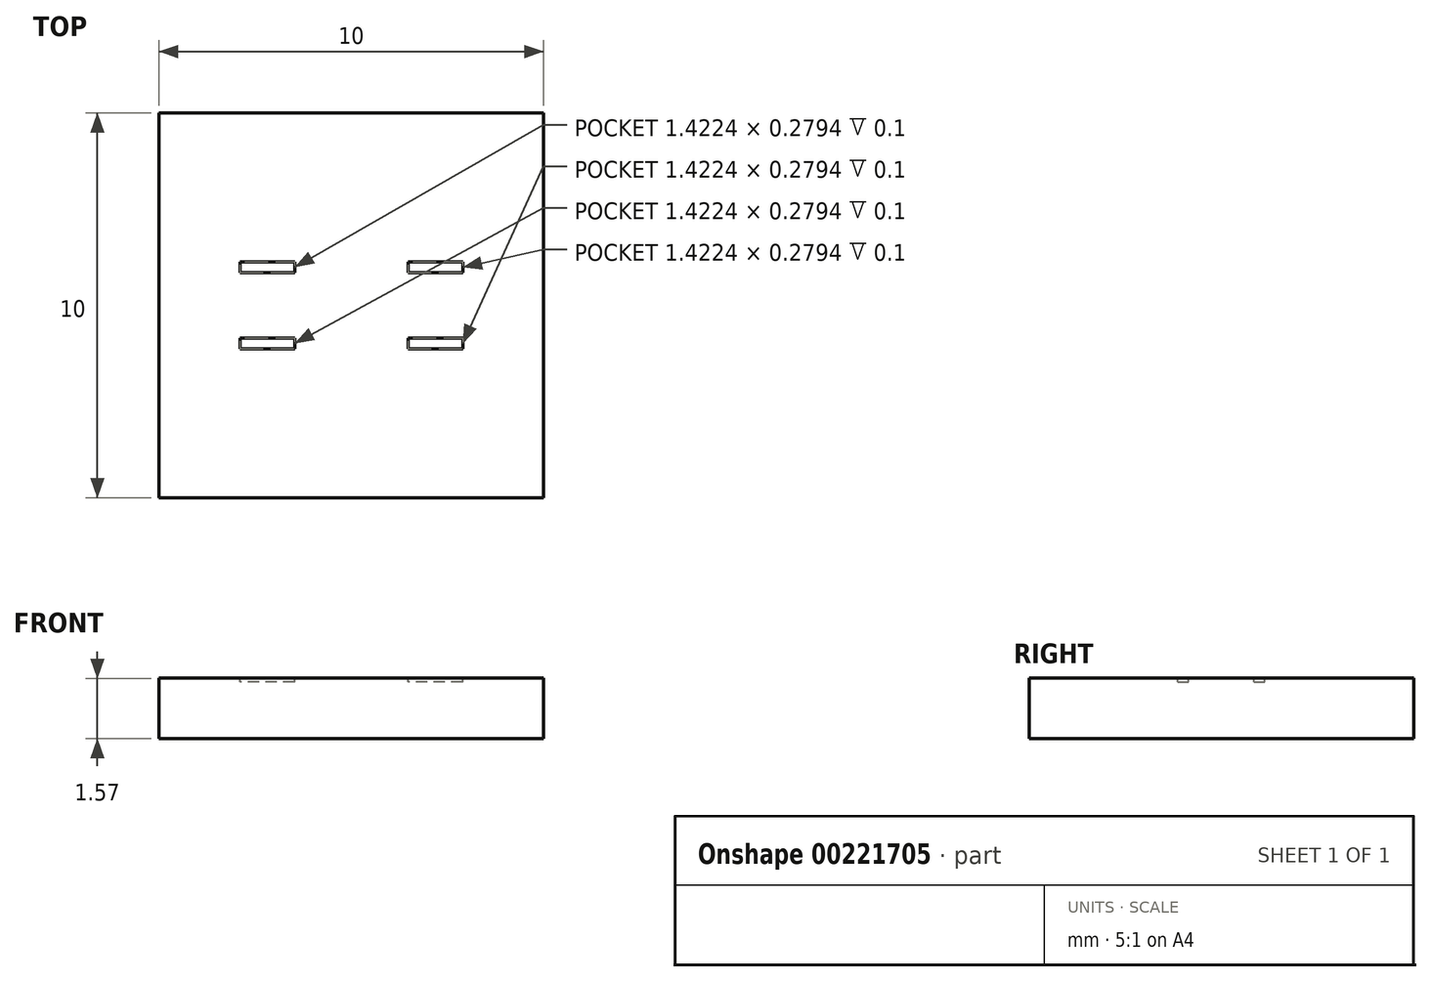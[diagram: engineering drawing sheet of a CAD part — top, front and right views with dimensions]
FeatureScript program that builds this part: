
annotation { "Feature Type Name" : "Feature", "Feature Type Description" : "" }
export const myFeature = defineFeature(function(context is Context, id is Id, definition is map)
    precondition{}
    {
        {
            var Q0;
            Q0=qCreatedBy(makeId("Top.planeOp"),FACE);
            var sketch = newSketch(context, id + "F0", { "sketchPlane" : qUnion([Q0])});
            skLineSegment(sketch, "E0.bottom", {"start": v(5, 5) * mm, "end": v(-5, 5) * mm});
            skLineSegment(sketch, "E0.top", {"start": v(5, -5) * mm, "end": v(-5, -5) * mm});
            skLineSegment(sketch, "E0.left", {"start": v(5, 5) * mm, "end": v(5, -5) * mm});
            skLineSegment(sketch, "E0.right", {"start": v(-5, 5) * mm, "end": v(-5, -5) * mm});
            skPoint(sketch, "E0.middle", {"position": v(0, 0) * mm});
            skSolve(sketch);
        }
        {
            var Q0;
            Q0 = qSketchRegion(id + "F0", true);
            extrude(context, id + "F1", {"entities" : qUnion([Q0]), "depth" : 1.57 * mm});
        }
        {
            var Q0;
            Q0=makeQuery(id+"F1.opExtrude","CAP_FACE",FACE,{"disambiguationData":[OSD([sQuery(id+"F0.wireOp",EDGE,"E0.bottom"),sQuery(id+"F0.wireOp",EDGE,"E0.top"),sQuery(id+"F0.wireOp",EDGE,"E0.left"),sQuery(id+"F0.wireOp",EDGE,"E0.right")])],"isStart":false});
            var sketch = newSketch(context, id + "F2", { "sketchPlane" : qUnion([Q0])});
            skLineSegment(sketch, "E1.bottom", {"start": v(-1.47, 0.85) * mm, "end": v(-2.9, 0.85) * mm});
            skLineSegment(sketch, "E1.top", {"start": v(-1.47, 1.13) * mm, "end": v(-2.9, 1.13) * mm});
            skLineSegment(sketch, "E1.left", {"start": v(-1.47, 0.85) * mm, "end": v(-1.47, 1.13) * mm});
            skLineSegment(sketch, "E1.right", {"start": v(-2.9, 0.85) * mm, "end": v(-2.9, 1.13) * mm});
            skPoint(sketch, "E1.middle", {"position": v(-2.18, 1) * mm});
            skLineSegment(sketch, "E2.bottom", {"start": v(2.9, 0.85) * mm, "end": v(1.47, 0.85) * mm});
            skLineSegment(sketch, "E2.top", {"start": v(2.9, 1.13) * mm, "end": v(1.47, 1.13) * mm});
            skLineSegment(sketch, "E2.left", {"start": v(2.9, 0.85) * mm, "end": v(2.9, 1.13) * mm});
            skLineSegment(sketch, "E2.right", {"start": v(1.47, 0.85) * mm, "end": v(1.47, 1.13) * mm});
            skPoint(sketch, "E2.middle", {"position": v(2.18, 1) * mm});
            skLineSegment(sketch, "E3.bottom", {"start": v(-1.47, -1.13) * mm, "end": v(-2.9, -1.13) * mm});
            skLineSegment(sketch, "E3.top", {"start": v(-1.47, -0.85) * mm, "end": v(-2.9, -0.85) * mm});
            skLineSegment(sketch, "E3.left", {"start": v(-1.47, -1.13) * mm, "end": v(-1.47, -0.85) * mm});
            skLineSegment(sketch, "E3.right", {"start": v(-2.9, -1.13) * mm, "end": v(-2.9, -0.85) * mm});
            skPoint(sketch, "E3.middle", {"position": v(-2.18, -1) * mm});
            skLineSegment(sketch, "E4.bottom", {"start": v(2.9, -1.13) * mm, "end": v(1.47, -1.13) * mm});
            skLineSegment(sketch, "E4.top", {"start": v(2.9, -0.85) * mm, "end": v(1.47, -0.85) * mm});
            skLineSegment(sketch, "E4.left", {"start": v(2.9, -1.13) * mm, "end": v(2.9, -0.85) * mm});
            skLineSegment(sketch, "E4.right", {"start": v(1.47, -1.13) * mm, "end": v(1.47, -0.85) * mm});
            skPoint(sketch, "E4.middle", {"position": v(2.18, -1) * mm});
            skLineSegment(sketch, "E5", {"start": v(-2.18, 1) * mm, "end": v(0, 0) * mm, "construction": true});
            skLineSegment(sketch, "E6", {"start": v(0, 0) * mm, "end": v(2.18, 1) * mm, "construction": true});
            skLineSegment(sketch, "E7", {"start": v(0, 0) * mm, "end": v(-2.18, -1) * mm, "construction": true});
            skSolve(sketch);
        }
        {
            var Q0;
            Q0 = qSketchRegion(id + "F2", true);
            extrude(context, id + "F3", {"entities" : qUnion([Q0]), "operationType" : NewBodyOperationType.REMOVE, "oppositeDirection" : true, "depth" : .1 * mm});
        }
    });
